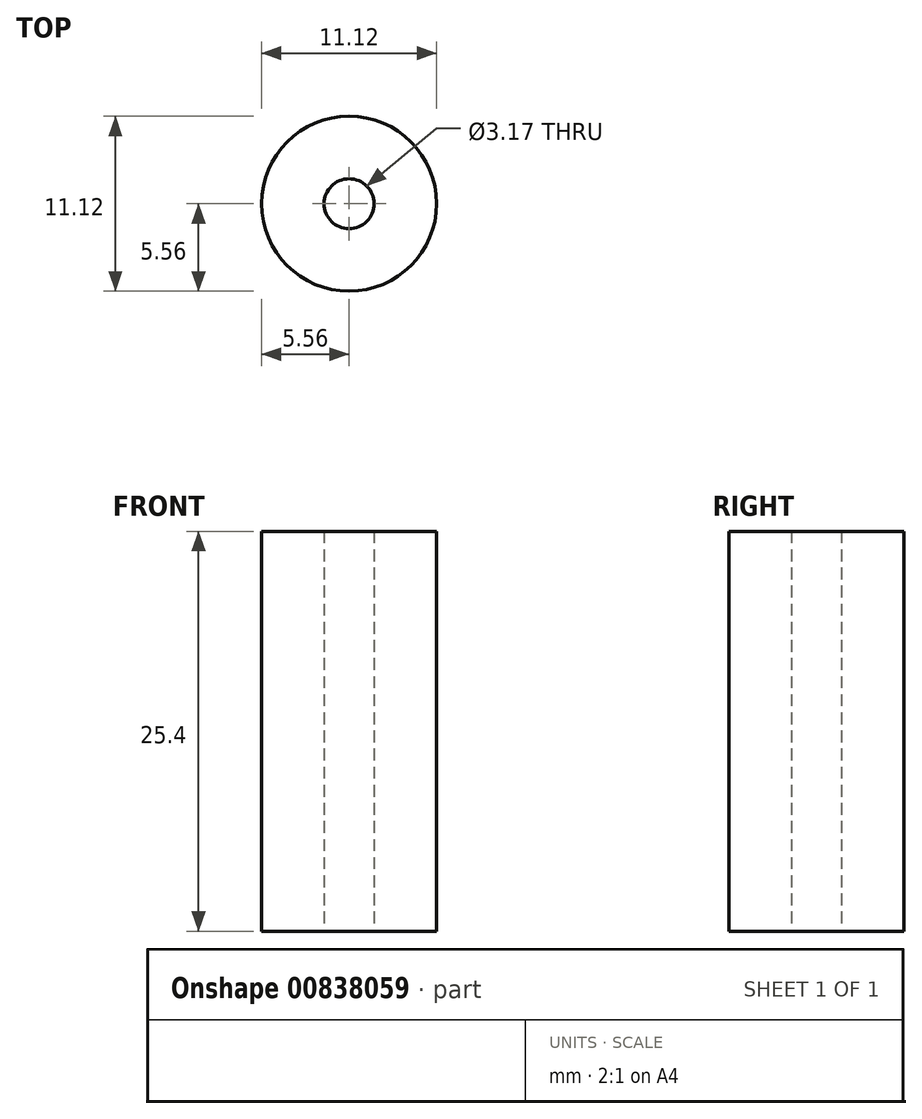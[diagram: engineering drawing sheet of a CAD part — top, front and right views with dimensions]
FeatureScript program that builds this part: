
annotation { "Feature Type Name" : "Feature", "Feature Type Description" : "" }
export const myFeature = defineFeature(function(context is Context, id is Id, definition is map)
    precondition{}
    {
        {
            var Q0;
            Q0=qCreatedBy(makeId("Top.planeOp"),FACE);
            var sketch = newSketch(context, id + "F0", { "sketchPlane" : qUnion([Q0])});
            skCircle(sketch, "E0", {"center": v(0, 0) * mm, "radius": 5.56 * mm});
            skCircle(sketch, "E1", {"center": v(0, 0) * mm, "radius": 1.59 * mm});
            skSolve(sketch);
        }
        {
            var Q0;
            Q0=makeQuery(id+"F0.imprint","IMPRINT",FACE,{"disambiguationData":[TD([[makeQuery(id+"F0.imprint","IMPRINT",EDGE,{"derivedFrom":sQuery(id+"F0.wireOp",EDGE,"E0")}),1.0]])]});
            extrude(context, id + "F1", {"entities" : qUnion([Q0]), "depth" : 25.4 * mm, "offsetDistance" : 25.4 * mm});
        }
    });
